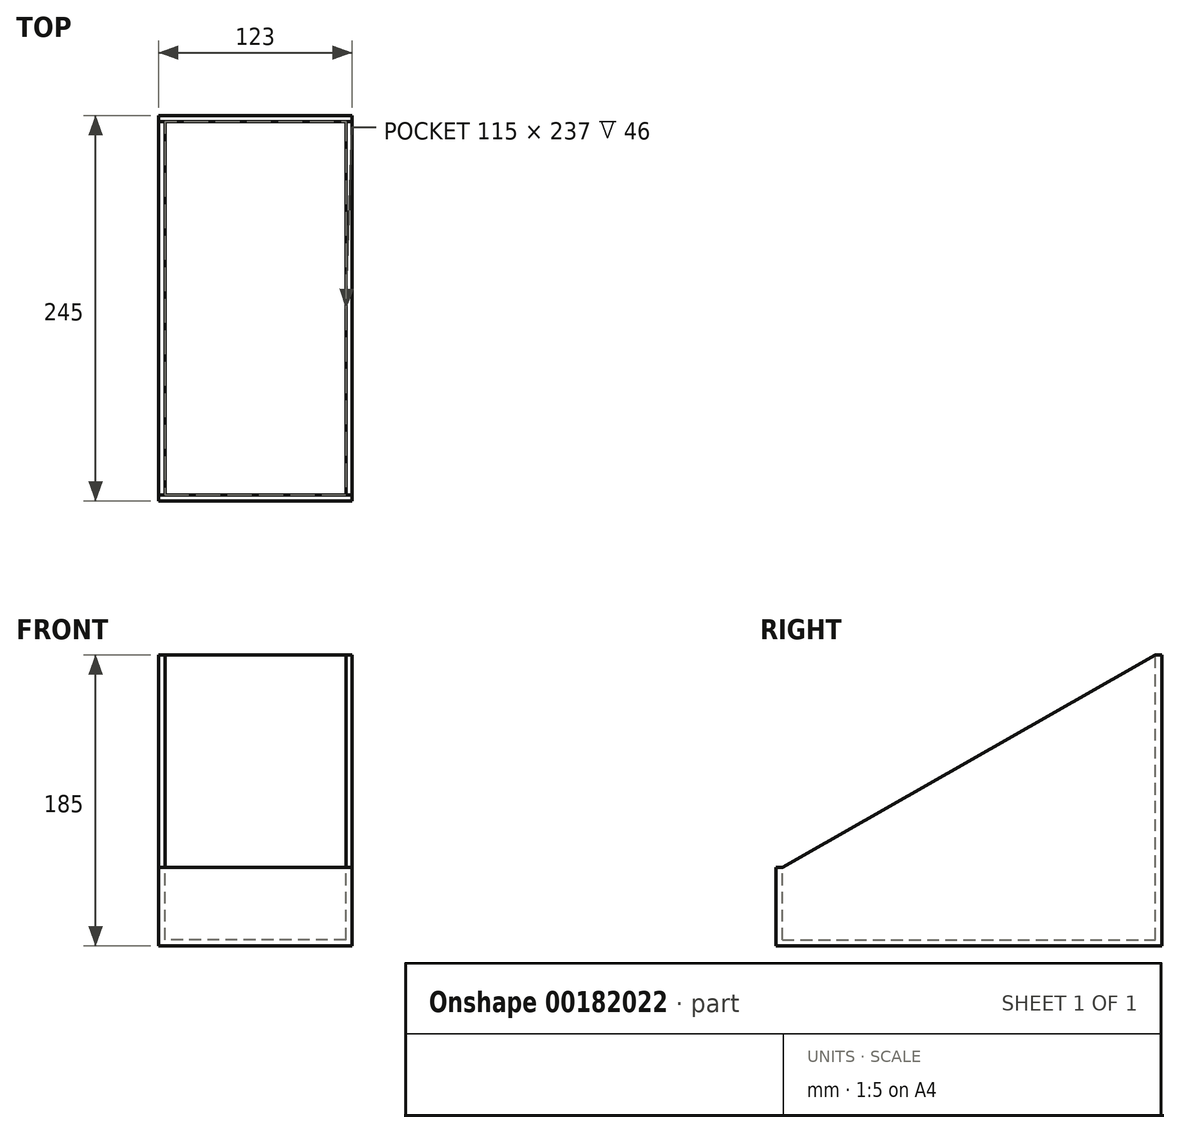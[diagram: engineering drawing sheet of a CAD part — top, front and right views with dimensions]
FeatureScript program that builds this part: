
annotation { "Feature Type Name" : "Feature", "Feature Type Description" : "" }
export const myFeature = defineFeature(function(context is Context, id is Id, definition is map)
    precondition{}
    {
        {
            var Q0;
            Q0=qCreatedBy(makeId("Front.planeOp"),FACE);
            var sketch = newSketch(context, id + "F0", { "sketchPlane" : qUnion([Q0])});
            skLineSegment(sketch, "E0.bottom", {"start": v(0, 0) * mm, "end": v(-123, 0) * mm});
            skLineSegment(sketch, "E0.top", {"start": v(0, 185) * mm, "end": v(-123, 185) * mm});
            skLineSegment(sketch, "E0.left", {"start": v(0, 0) * mm, "end": v(0, 185) * mm});
            skLineSegment(sketch, "E0.right", {"start": v(-123, 0) * mm, "end": v(-123, 185) * mm});
            skSolve(sketch);
        }
        {
            var Q0;
            Q0=qSketchRegion(id+"F0",true);
            extrude(context, id + "F1", {"entities" : qUnion([Q0]), "oppositeDirection" : true, "depth" : 245 * mm});
        }
        {
            var Q0;
            Q0=qCreatedBy(makeId("Right.planeOp"),FACE);
            var sketch = newSketch(context, id + "F2", { "sketchPlane" : qUnion([Q0])});
            skLineSegment(sketch, "E1.0", {"start": v(245, 185) * mm, "end": v(0, 185) * mm, "construction": true});
            skLineSegment(sketch, "E2", {"start": v(0, 185) * mm, "end": v(0, 50) * mm});
            skLineSegment(sketch, "E3", {"start": v(0, 50) * mm, "end": v(4, 50) * mm});
            skLineSegment(sketch, "E4", {"start": v(4, 50) * mm, "end": v(241, 185) * mm});
            skLineSegment(sketch, "E5", {"start": v(241, 185) * mm, "end": v(0, 185) * mm});
            skSolve(sketch);
        }
        {
            var Q0;
            Q0=makeQuery(id+"F2.imprint","IMPRINT",FACE,{"disambiguationData":[TD([[makeQuery(id+"F2.imprint","IMPRINT",EDGE,{"derivedFrom":sQuery(id+"F2.wireOp",EDGE,"E2")}),1.0]])]});
            extrude(context, id + "F3", {"entities" : qUnion([Q0]), "operationType" : NewBodyOperationType.REMOVE, "endBound" : BoundingType.UP_TO_NEXT, "oppositeDirection" : true, "depth" : 25 * mm});
        }
        {
            var Q0;
            Q0=qCreatedBy(makeId("Top.planeOp"),FACE);
            cPlane(context, id + "F4", {"entities" : qUnion([Q0]), "cplaneType" : CPlaneType.OFFSET, "offset" : 200 * mm, "width" : 150 * mm, "height" : 150 * mm});
        }
        {
            var Q0;
            Q0=qCreatedBy(id+"F4.planeOp",FACE);
            var sketch = newSketch(context, id + "F5", { "sketchPlane" : qUnion([Q0])});
            skLineSegment(sketch, "E6.0.0", {"start": v(-123, 241) * mm, "end": v(-123, 4) * mm, "construction": true});
            skLineSegment(sketch, "E6.0.1", {"start": v(-123, 4) * mm, "end": v(0, 4) * mm, "construction": true});
            skLineSegment(sketch, "E6.0.2", {"start": v(0, 4) * mm, "end": v(0, 241) * mm, "construction": true});
            skLineSegment(sketch, "E6.0.3", {"start": v(0, 241) * mm, "end": v(-123, 241) * mm, "construction": true});
            skLineSegment(sketch, "E7.0", {"start": v(-4, 4) * mm, "end": v(-4, 366) * mm, "construction": true});
            skLineSegment(sketch, "E8.0", {"start": v(-119, 241) * mm, "end": v(-119, 4) * mm, "construction": true});
            skLineSegment(sketch, "E9.bottom", {"start": v(-4, 4) * mm, "end": v(-119, 4) * mm});
            skLineSegment(sketch, "E9.top", {"start": v(-4, 241) * mm, "end": v(-119, 241) * mm});
            skLineSegment(sketch, "E9.left", {"start": v(-4, 4) * mm, "end": v(-4, 241) * mm});
            skLineSegment(sketch, "E9.right", {"start": v(-119, 4) * mm, "end": v(-119, 241) * mm});
            skSolve(sketch);
        }
        {
            var Q0;
            Q0=qSketchRegion(id+"F5",true);
            extrude(context, id + "F6", {"entities" : qUnion([Q0]), "operationType" : NewBodyOperationType.REMOVE, "oppositeDirection" : true, "depth" : 196 * mm});
        }
    });
